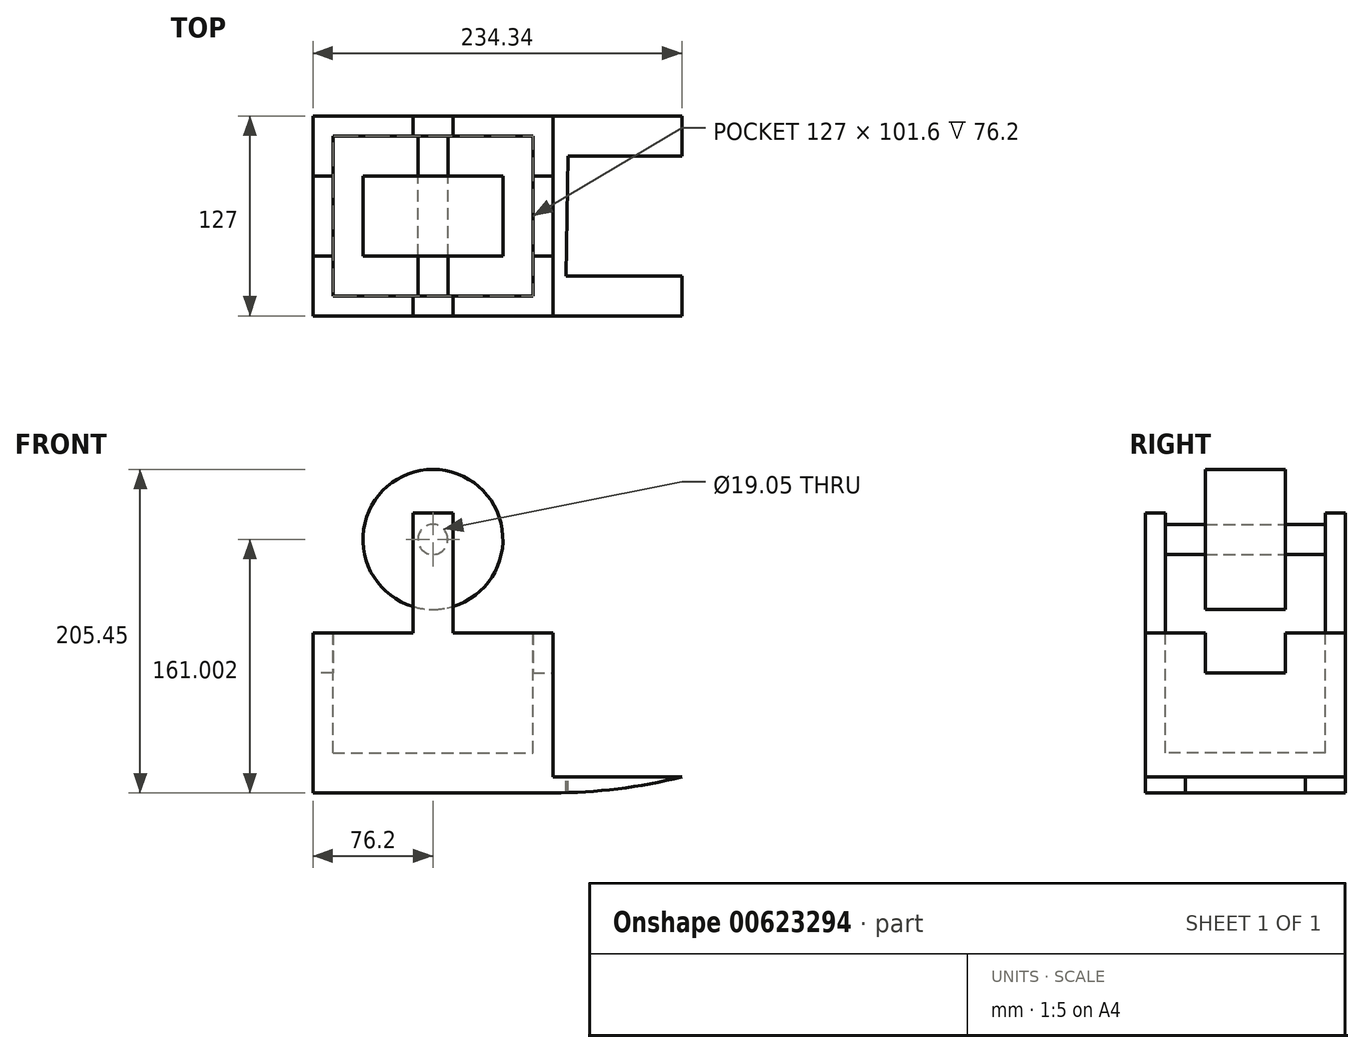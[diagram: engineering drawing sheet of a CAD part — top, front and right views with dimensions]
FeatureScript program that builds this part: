
annotation { "Feature Type Name" : "Feature", "Feature Type Description" : "" }
export const myFeature = defineFeature(function(context is Context, id is Id, definition is map)
    precondition{}
    {
        {
            var Q0;
            Q0=qCreatedBy(makeId("Front.planeOp"),FACE);
            var sketch = newSketch(context, id + "F0", { "sketchPlane" : qUnion([Q0])});
            skLineSegment(sketch, "E0", {"start": v(0, 0) * mm, "end": v(0, 101.6) * mm});
            skLineSegment(sketch, "E1", {"start": v(0, 101.6) * mm, "end": v(152.4, 101.6) * mm});
            skLineSegment(sketch, "E2", {"start": v(152.4, 101.6) * mm, "end": v(152.4, 0) * mm});
            skLineSegment(sketch, "E3", {"start": v(152.4, 0) * mm, "end": v(0, 0) * mm});
            skArc(sketch, "E4", {"start": v(152.4, 0) * mm, "mid": v(193.69, 2.56) * mm, "end": v(234.34, 10.2) * mm});
            skLineSegment(sketch, "E5", {"start": v(234.34, 10.2) * mm, "end": v(152.4, 10.2) * mm});
            skSolve(sketch);
        }
        {
            var Q0;
            Q0=makeQuery(id+"F0.imprint","IMPRINT",FACE,{"disambiguationData":[TD([[makeQuery(id+"F0.imprint","IMPRINT",EDGE,{"derivedFrom":sQuery(id+"F0.wireOp",EDGE,"E0")}),-1.0]])]});
            var Q1;
            {var subQ0=sQuery(id+"F0.wireOp",EDGE,"E4");Q1=makeQuery(id+"F0.imprint","IMPRINT",FACE,{"disambiguationData":[TD([[makeQuery(id+"F0.imprint","IMPRINT",EDGE,{"derivedFrom":subQ0}),1.0]])]});}
            extrude(context, id + "F1", {"entities" : qUnion([Q0, Q1]), "depth" : 127 * mm, "offsetDistance" : 25.4 * mm});
        }
        {
            var Q0;
            Q0=makeQuery(id+"F1.opExtrude","SWEPT_FACE",FACE,{"disambiguationData":[OSD([sQuery(id+"F0.wireOp",EDGE,"E1")])]});
            var sketch = newSketch(context, id + "F2", { "sketchPlane" : qUnion([Q0])});
            skLineSegment(sketch, "E6", {"start": v(12.7, -12.7) * mm, "end": v(12.7, -114.3) * mm});
            skLineSegment(sketch, "E7", {"start": v(12.7, -114.3) * mm, "end": v(139.7, -114.3) * mm});
            skLineSegment(sketch, "E8", {"start": v(139.7, -114.3) * mm, "end": v(139.7, -12.7) * mm});
            skLineSegment(sketch, "E9", {"start": v(12.7, -12.7) * mm, "end": v(139.7, -12.7) * mm});
            skSolve(sketch);
        }
        {
            var Q0;
            Q0=makeQuery(id+"F2.imprint","IMPRINT",FACE,{"disambiguationData":[TD([[makeQuery(id+"F2.imprint","IMPRINT",EDGE,{"derivedFrom":sQuery(id+"F2.wireOp",EDGE,"E6")}),1.0]])]});
            extrude(context, id + "F3", {"entities" : qUnion([Q0]), "operationType" : NewBodyOperationType.REMOVE, "oppositeDirection" : true, "depth" : 76.2 * mm, "offsetDistance" : 25.4 * mm});
        }
        {
            var Q0;
            Q0=makeQuery(id+"F1.opExtrude","SWEPT_FACE",FACE,{"disambiguationData":[OSD([sQuery(id+"F0.wireOp",EDGE,"E2")])]});
            var sketch = newSketch(context, id + "F4", { "sketchPlane" : qUnion([Q0])});
            skPoint(sketch, "E10", {"position": v(-63.5, 101.6) * mm});
            skLineSegment(sketch, "E11", {"start": v(-63.5, 101.6) * mm, "end": v(-38.1, 101.6) * mm});
            skLineSegment(sketch, "E12", {"start": v(-38.1, 101.6) * mm, "end": v(-88.9, 101.6) * mm});
            skLineSegment(sketch, "E13", {"start": v(-88.9, 101.6) * mm, "end": v(-88.9, 76.2) * mm});
            skLineSegment(sketch, "E14", {"start": v(-88.9, 76.2) * mm, "end": v(-38.1, 76.2) * mm});
            skLineSegment(sketch, "E15", {"start": v(-38.1, 76.2) * mm, "end": v(-38.1, 101.6) * mm});
            skSolve(sketch);
        }
        {
            var Q0;
            {var subQ0=sQuery(id+"F4.wireOp",EDGE,"E13");Q0=makeQuery(id+"F4.imprint","IMPRINT",FACE,{"disambiguationData":[TD([[makeQuery(id+"F4.imprint","IMPRINT",EDGE,{"derivedFrom":subQ0}),1.0]])]});}
            extrude(context, id + "F5", {"entities" : qUnion([Q0]), "operationType" : NewBodyOperationType.REMOVE, "oppositeDirection" : true, "depth" : 25.4 * mm, "offsetDistance" : 25.4 * mm});
        }
        {
            var Q0;
            Q0=makeQuery(id+"F1.opExtrude","SWEPT_FACE",FACE,{"disambiguationData":[OSD([sQuery(id+"F0.wireOp",EDGE,"E0")])]});
            var sketch = newSketch(context, id + "F6", { "sketchPlane" : qUnion([Q0])});
            skPoint(sketch, "E16", {"position": v(63.5, 101.6) * mm});
            skLineSegment(sketch, "E17", {"start": v(63.5, 101.6) * mm, "end": v(88.9, 101.6) * mm});
            skLineSegment(sketch, "E18", {"start": v(88.9, 101.6) * mm, "end": v(38.1, 101.6) * mm});
            skLineSegment(sketch, "E19", {"start": v(38.1, 101.6) * mm, "end": v(38.1, 76.2) * mm});
            skLineSegment(sketch, "E20", {"start": v(38.1, 76.2) * mm, "end": v(88.9, 76.2) * mm});
            skLineSegment(sketch, "E21", {"start": v(88.9, 76.2) * mm, "end": v(88.9, 101.6) * mm});
            skSolve(sketch);
        }
        {
            var Q0;
            {var subQ3=sQuery(id+"F6.wireOp",EDGE,"E19");Q0=makeQuery(id+"F6.imprint","IMPRINT",FACE,{"disambiguationData":[TD([[makeQuery(id+"F6.imprint","IMPRINT",EDGE,{"derivedFrom":subQ3}),1.0]])]});}
            extrude(context, id + "F7", {"entities" : qUnion([Q0]), "operationType" : NewBodyOperationType.REMOVE, "oppositeDirection" : true, "depth" : 25.4 * mm, "offsetDistance" : 25.4 * mm});
        }
        {
            var Q0;
            {var subQ1=sQuery(id+"F0.wireOp",EDGE,"E1");Q0=makeQuery(id+"F7.boolean.opBoolean","SPLIT",FACE,{"disambiguationData":[TD([makeQuery(id+"F3.boolean.opBoolean","COPY",FACE,{"derivedFrom":makeQuery(id+"F3.opExtrude","SWEPT_FACE",FACE,{"disambiguationData":[OSD([sQuery(id+"F2.wireOp",EDGE,"E7")])]})})])],"derivedFrom":makeQuery(id+"F1.opExtrude","SWEPT_FACE",FACE,{"disambiguationData":[OSD([subQ1])]})});}
            var sketch = newSketch(context, id + "F8", { "sketchPlane" : qUnion([Q0])});
            skLineSegment(sketch, "E22", {"start": v(76.2, -127) * mm, "end": v(63.5, -127) * mm});
            skLineSegment(sketch, "E23", {"start": v(63.5, -127) * mm, "end": v(63.5, -114.3) * mm});
            skLineSegment(sketch, "E24", {"start": v(63.5, -114.3) * mm, "end": v(88.9, -114.3) * mm});
            skLineSegment(sketch, "E25", {"start": v(88.9, -114.3) * mm, "end": v(88.9, -127) * mm});
            skLineSegment(sketch, "E26", {"start": v(88.9, -127) * mm, "end": v(76.2, -127) * mm});
            skLineSegment(sketch, "E27", {"start": v(63.5, -127) * mm, "end": v(0, -127) * mm});
            skLineSegment(sketch, "E28", {"start": v(88.9, -127) * mm, "end": v(152.4, -127) * mm});
            skLineSegment(sketch, "E29", {"start": v(0, 0) * mm, "end": v(63.5, 0) * mm});
            skLineSegment(sketch, "E30", {"start": v(63.5, 0) * mm, "end": v(88.9, 0) * mm});
            skLineSegment(sketch, "E31", {"start": v(88.9, 0) * mm, "end": v(152.4, 0) * mm});
            skLineSegment(sketch, "E32", {"start": v(63.5, 0) * mm, "end": v(63.5, -12.7) * mm});
            skLineSegment(sketch, "E33", {"start": v(63.5, -12.7) * mm, "end": v(88.9, -12.7) * mm});
            skLineSegment(sketch, "E34", {"start": v(88.9, -12.7) * mm, "end": v(88.9, 0) * mm});
            skSolve(sketch);
        }
        {
            var Q0;
            Q0=makeQuery(id+"F8.imprint","IMPRINT",FACE,{"disambiguationData":[TD([[makeQuery(id+"F8.imprint","IMPRINT",EDGE,{"derivedFrom":sQuery(id+"F8.wireOp",EDGE,"E22")}),1.0]])]});
            var Q1;
            Q1=makeQuery(id+"F8.imprint","IMPRINT",FACE,{"disambiguationData":[TD([[makeQuery(id+"F8.imprint","IMPRINT",EDGE,{"derivedFrom":sQuery(id+"F8.wireOp",EDGE,"E30")}),-1.0]])]});
            extrude(context, id + "F9", {"entities" : qUnion([Q0, Q1]), "operationType" : NewBodyOperationType.ADD, "depth" : 76.2 * mm, "offsetDistance" : 25.4 * mm});
        }
        {
            var Q0;
            Q0=makeQuery(id+"F1.opExtrude","SWEPT_FACE",FACE,{"disambiguationData":[OSD([sQuery(id+"F0.wireOp",EDGE,"E5")])]});
            var sketch = newSketch(context, id + "F10", { "sketchPlane" : qUnion([Q0])});
            skLineSegment(sketch, "E35", {"start": v(160.82, -101.6) * mm, "end": v(198.39, -101.6) * mm});
            skLineSegment(sketch, "E36", {"start": v(198.39, -25.4) * mm, "end": v(162.15, -25.4) * mm});
            skLineSegment(sketch, "E37", {"start": v(162.15, -25.4) * mm, "end": v(160.82, -101.6) * mm});
            skLineSegment(sketch, "E38", {"start": v(198.39, -101.6) * mm, "end": v(234.34, -101.6) * mm});
            skLineSegment(sketch, "E39", {"start": v(234.34, -101.6) * mm, "end": v(234.34, -25.4) * mm});
            skLineSegment(sketch, "E40", {"start": v(234.34, -25.4) * mm, "end": v(198.39, -25.4) * mm});
            skSolve(sketch);
        }
        {
            var Q0;
            Q0=makeQuery(id+"F10.imprint","IMPRINT",FACE,{"disambiguationData":[TD([[makeQuery(id+"F10.imprint","IMPRINT",EDGE,{"derivedFrom":sQuery(id+"F10.wireOp",EDGE,"E35")}),1.0]])]});
            extrude(context, id + "F11", {"entities" : qUnion([Q0]), "operationType" : NewBodyOperationType.REMOVE, "oppositeDirection" : true, "depth" : 25.4 * mm, "offsetDistance" : 25.4 * mm});
        }
        {
            var Q0;
            Q0=makeQuery(id+"F9.boolean.opBoolean","MERGE",FACE,{"derivedFrom":[makeQuery(id+"F3.boolean.opBoolean","COPY",FACE,{"derivedFrom":makeQuery(id+"F3.opExtrude","SWEPT_FACE",FACE,{"disambiguationData":[OSD([sQuery(id+"F2.wireOp",EDGE,"E9")])]})}),makeQuery(id+"F9.opExtrude","SWEPT_FACE",FACE,{"disambiguationData":[OSD([sQuery(id+"F8.wireOp",EDGE,"E33")])]})]});
            var sketch = newSketch(context, id + "F12", { "sketchPlane" : qUnion([Q0])});
            skCircle(sketch, "E41", {"center": v(76.2, 161) * mm, "radius": 9.53 * mm});
            skPoint(sketch, "E41.centerSnap0", {"position": v(76.2, 177.8) * mm});
            skSolve(sketch);
        }
        {
            var Q0;
            Q0=makeQuery(id+"F12.imprint","IMPRINT",FACE,{"disambiguationData":[TD([[makeQuery(id+"F12.imprint","IMPRINT",EDGE,{"derivedFrom":sQuery(id+"F12.wireOp",EDGE,"E41")}),1.0]])]});
            extrude(context, id + "F13", {"entities" : qUnion([Q0]), "endBound" : BoundingType.UP_TO_NEXT, "depth" : 25.4 * mm, "offsetDistance" : 25.4 * mm});
        }
        {
            var Q0;
            Q0=qCreatedBy(makeId("Front.planeOp"),FACE);
            cPlane(context, id + "F14", {"entities" : qUnion([Q0]), "cplaneType" : CPlaneType.OFFSET, "offset" : 63.5 * mm, "width" : 152.4 * mm, "height" : 152.4 * mm});
        }
        {
            var Q0;
            Q0=qCreatedBy(id+"F14.planeOp",FACE);
            var sketch = newSketch(context, id + "F15", { "sketchPlane" : qUnion([Q0])});
            skCircle(sketch, "E42.0", {"center": v(76.2, 161) * mm, "radius": 9.53 * mm});
            skCircle(sketch, "E43", {"center": v(76.2, 161) * mm, "radius": 44.45 * mm});
            skSolve(sketch);
        }
        {
            var Q0;
            Q0 = qSketchRegion(id + "F15", true);
            extrude(context, id + "F16", {"entities" : qUnion([Q0]), "endBound" : BoundingType.SYMMETRIC, "depth" : 50.8 * mm, "offsetDistance" : 25.4 * mm});
        }
    });
